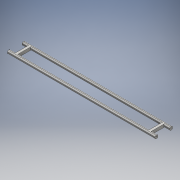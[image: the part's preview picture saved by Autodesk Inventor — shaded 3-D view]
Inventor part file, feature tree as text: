
AUTODESK INVENTOR PART (.ipt)
format: ipt  version: 2016 (Build 200138000, 138)  size: 161,280 bytes
history: native  units: mm
features: fillet x3, extrude x2, sketch x2
ambient origin geometry x8: Origin, YZ Plane, XZ Plane, XY Plane, X Axis, Y Axis, Z Axis, Center Point
bodies: 实体1 (feature_tree)
feature tree (7):
  extrude  "拉伸1"  Depth=15.0mm
  fillet  "圆角1"  Radius=15.0mm
  fillet  "圆角2"  Radius=7.5mm
  fillet  "圆角3"  Radius=75.0mm
  extrude  "拉伸2"  Depth=12.0mm
  sketch  "草图1"  dims[d0=755.0mm d1=15.0mm d2=15.0mm d3=7.5mm d4=75.0mm]
  sketch  "草图2"  dims[d5=12.0mm d6=12.0mm d7=30.0mm d8=30.0mm d9=15.0mm d10=0.0mm d11=5.0mm d12=5.0mm d13=5.0mm d14=7.5mm d15=7.5mm d16=7.5mm d17=7.5mm d18=5.0mm d19=800.0mm d20=0.0mm]
